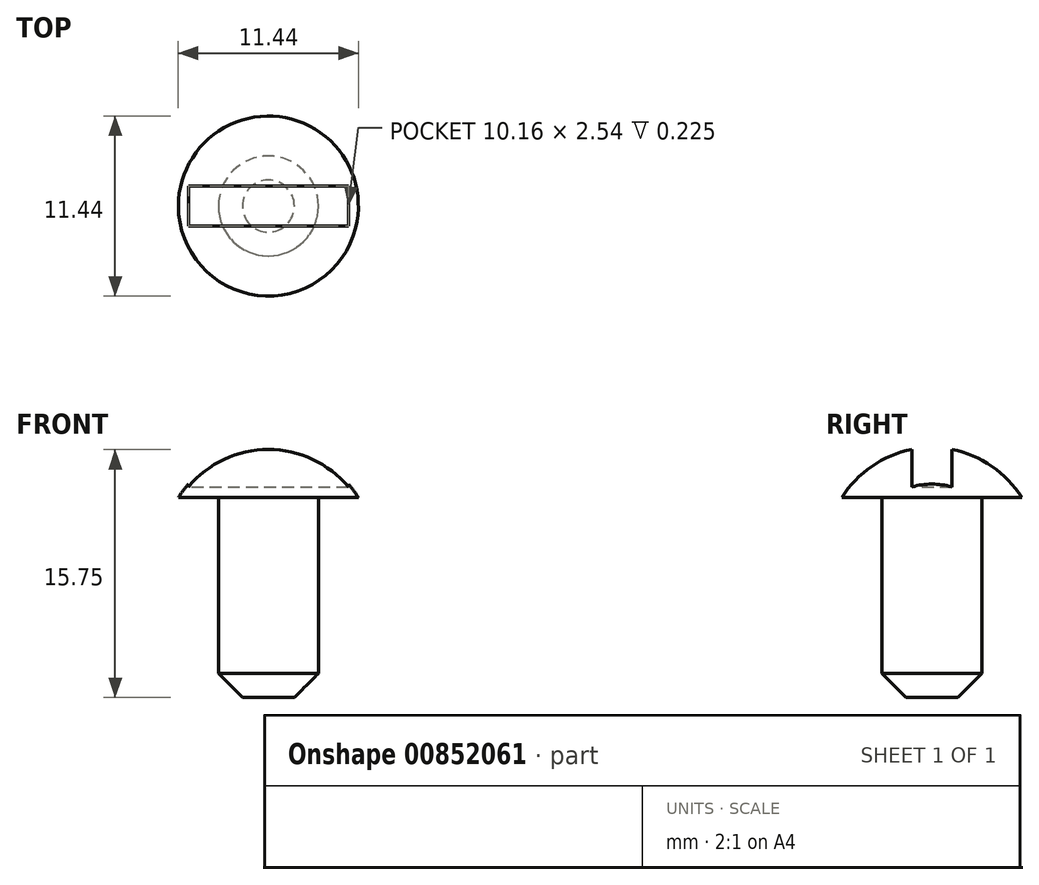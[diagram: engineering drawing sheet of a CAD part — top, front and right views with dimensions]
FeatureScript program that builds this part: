
annotation { "Feature Type Name" : "Feature", "Feature Type Description" : "" }
export const myFeature = defineFeature(function(context is Context, id is Id, definition is map)
    precondition{}
    {
        {
            var Q0;
            Q0=qCreatedBy(makeId("Front.planeOp"),FACE);
            var sketch = newSketch(context, id + "F0", { "sketchPlane" : qUnion([Q0])});
            skArc(sketch, "E0", {"start": v(0, 15.88) * mm, "mid": v(3.27, 15.03) * mm, "end": v(5.72, 12.7) * mm});
            skLineSegment(sketch, "E1", {"start": v(5.72, 12.7) * mm, "end": v(3.18, 12.7) * mm});
            skLineSegment(sketch, "E2", {"start": v(3.18, 12.7) * mm, "end": v(3.18, 0) * mm});
            skLineSegment(sketch, "E3", {"start": v(3.18, 0) * mm, "end": v(0, 0) * mm});
            skLineSegment(sketch, "E4", {"start": v(0, 0) * mm, "end": v(0, 15.88) * mm});
            skLineSegment(sketch, "E5", {"start": v(0, 0) * mm, "end": v(0, 34.22) * mm, "construction": true});
            skSolve(sketch);
        }
        {
            var Q0;
            Q0 = qSketchRegion(id + "F0", true);
            var Q1;
            Q1=sQuery(id+"F0.wireOp",EDGE,"E5");
            revolve(context, id + "F1", {"surfaceOperationType" : NewSurfaceOperationType.NEW, "entities" : qUnion([Q0]), "axis" : qUnion([Q1]), "revolveType" : RevolveType.FULL});
        }
        {
            var Q0;
            Q0=makeQuery(id+"F1.opRevolve","SWEPT_EDGE",EDGE,{"disambiguationData":[OSD([sQuery(id+"F0.wireOp",EDGE,"E2"),sQuery(id+"F0.wireOp",EDGE,"E3")])]});
            chamfer(context, id + "F2", {"entities" : qUnion([Q0]), "width" : 1.52 * mm, "tangentPropagation" : true});
        }
        {
            var Q0;
            Q0=qCreatedBy(makeId("Top.planeOp"),FACE);
            cPlane(context, id + "F3", {"entities" : qUnion([Q0]), "cplaneType" : CPlaneType.OFFSET, "offset" : 13.33 * mm, "width" : 152.4 * mm, "height" : 152.4 * mm});
        }
        {
            var Q0;
            Q0=qCreatedBy(id+"F3.planeOp",FACE);
            var sketch = newSketch(context, id + "F4", { "sketchPlane" : qUnion([Q0])});
            skLineSegment(sketch, "E6.bottom", {"start": v(5.08, 1.27) * mm, "end": v(-5.08, 1.27) * mm});
            skLineSegment(sketch, "E6.top", {"start": v(5.08, -1.27) * mm, "end": v(-5.08, -1.27) * mm});
            skLineSegment(sketch, "E6.left", {"start": v(5.08, 1.27) * mm, "end": v(5.08, -1.27) * mm});
            skLineSegment(sketch, "E6.right", {"start": v(-5.08, 1.27) * mm, "end": v(-5.08, -1.27) * mm});
            skPoint(sketch, "E6.middle", {"position": v(0, 0) * mm});
            skSolve(sketch);
        }
        {
            var Q0;
            Q0 = qSketchRegion(id + "F4", true);
            extrude(context, id + "F5", {"entities" : qUnion([Q0]), "operationType" : NewBodyOperationType.REMOVE, "endBound" : BoundingType.THROUGH_ALL, "depth" : 25.4 * mm, "offsetDistance" : 25.4 * mm});
        }
    });
